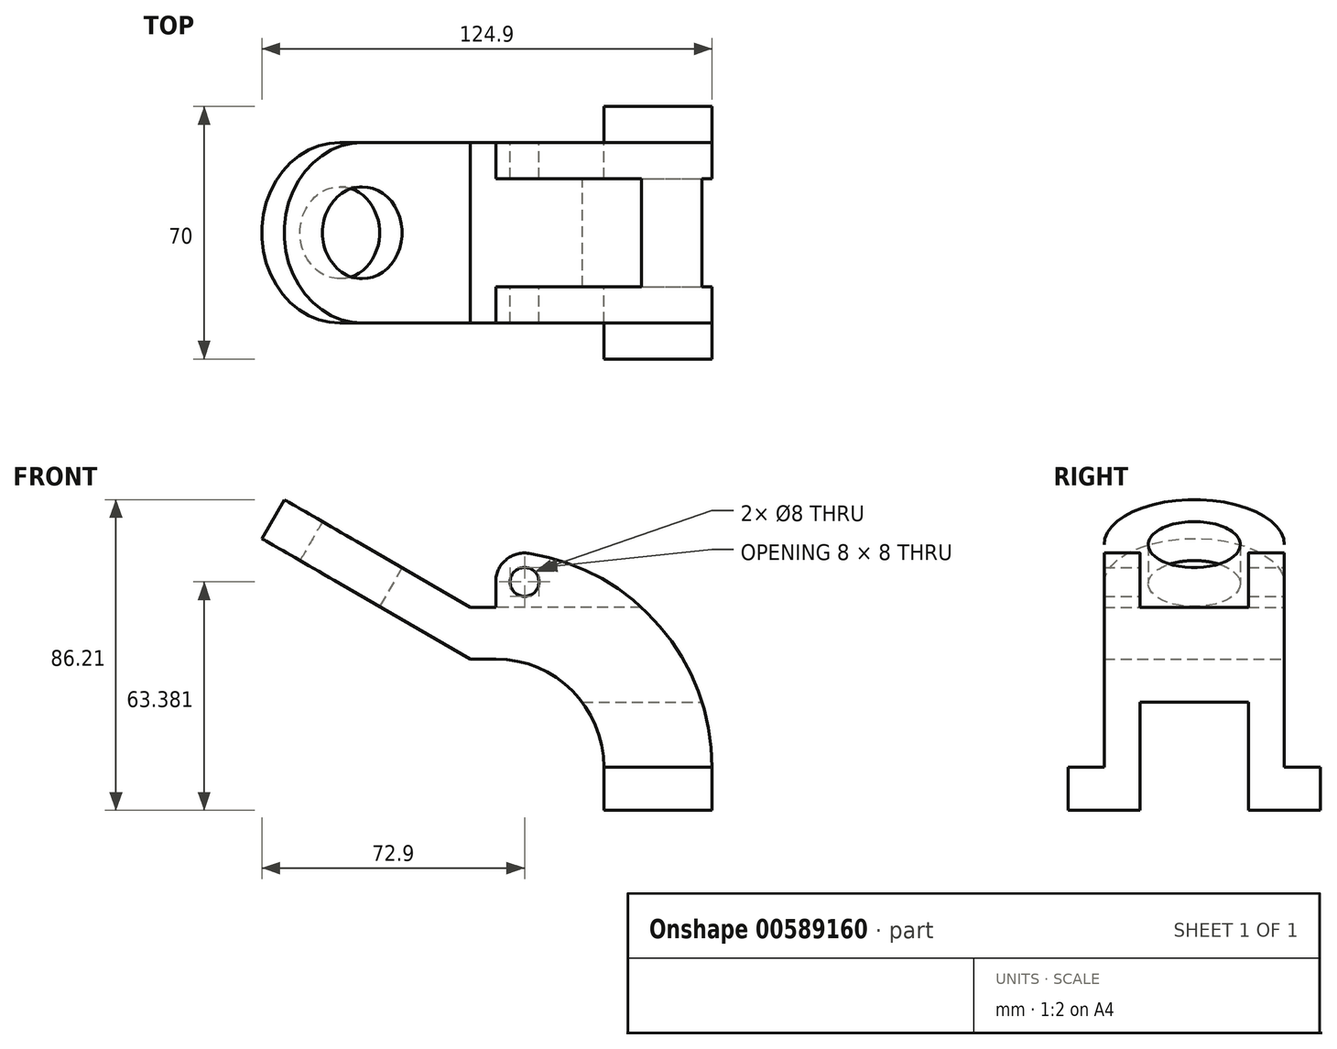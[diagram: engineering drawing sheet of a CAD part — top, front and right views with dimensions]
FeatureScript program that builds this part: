
annotation { "Feature Type Name" : "Feature", "Feature Type Description" : "" }
export const myFeature = defineFeature(function(context is Context, id is Id, definition is map)
    precondition{}
    {
        {
            var Q0;
            Q0=qCreatedBy(makeId("Front.planeOp"),FACE);
            var sketch = newSketch(context, id + "F0", { "sketchPlane" : qUnion([Q0])});
            skLineSegment(sketch, "E0", {"start": v(0, 0) * mm, "end": v(30, 0) * mm});
            skLineSegment(sketch, "E1", {"start": v(0, 0) * mm, "end": v(0, 12) * mm});
            skLineSegment(sketch, "E2", {"start": v(30, 0) * mm, "end": v(30, 12) * mm});
            skLineSegment(sketch, "E3", {"start": v(0, 12) * mm, "end": v(30, 12) * mm});
            skLineSegment(sketch, "E4", {"start": v(0, 12) * mm, "end": v(-30, 12) * mm, "construction": true});
            skLineSegment(sketch, "E5", {"start": v(-15, 12) * mm, "end": v(-15, 18) * mm, "construction": true});
            skArc(sketch, "E6", {"start": v(30, 12) * mm, "mid": v(15.57, 51.03) * mm, "end": v(-20.77, 71.29) * mm});
            skArc(sketch, "E7", {"start": v(0, 12) * mm, "mid": v(-8.79, 33.21) * mm, "end": v(-30, 42) * mm});
            skLineSegment(sketch, "E8", {"start": v(-30, 56.38) * mm, "end": v(-30, 63.38) * mm});
            skPoint(sketch, "E9.visualSharp", {"position": v(-30, 72) * mm});
            skArc(sketch, "E9.filletArc", {"start": v(-20.77, 71.29) * mm, "mid": v(-27.2, 69.46) * mm, "end": v(-30, 63.38) * mm});
            skPoint(sketch, "E10", {"position": v(-30, 56.38) * mm});
            skLineSegment(sketch, "E11", {"start": v(-30, 56.38) * mm, "end": v(-37, 56.38) * mm});
            skLineSegment(sketch, "E12", {"start": v(-30, 42) * mm, "end": v(-37, 42) * mm});
            skLineSegment(sketch, "E13", {"start": v(-37, 42) * mm, "end": v(-51.43, 42) * mm, "construction": true});
            skLineSegment(sketch, "E14", {"start": v(-37, 42) * mm, "end": v(-50, 49.5) * mm});
            skLineSegment(sketch, "E15", {"start": v(-37, 56.38) * mm, "end": v(-50, 63.88) * mm});
            skLineSegment(sketch, "E16", {"start": v(-37, 56.38) * mm, "end": v(-47.34, 56.38) * mm, "construction": true});
            skLineSegment(sketch, "E17", {"start": v(-50, 49.5) * mm, "end": v(-96.5, 76.35) * mm});
            skLineSegment(sketch, "E18", {"start": v(-50, 63.88) * mm, "end": v(-71.64, 76.38) * mm});
            skLineSegment(sketch, "E19", {"start": v(-71.64, 62) * mm, "end": v(-71.64, 76.38) * mm});
            skCircle(sketch, "E20", {"center": v(-22, 63.38) * mm, "radius": 4 * mm});
            skLineSegment(sketch, "E21", {"start": v(-71.64, 76.38) * mm, "end": v(-96.5, 76.38) * mm});
            skLineSegment(sketch, "E22", {"start": v(-96.5, 76.38) * mm, "end": v(-96.5, 62) * mm});
            skLineSegment(sketch, "E23", {"start": v(-96.5, 62) * mm, "end": v(-71.64, 62) * mm});
            skSolve(sketch);
        }
        {
            var Q0;
            Q0=makeQuery(id+"F0.imprint","IMPRINT",FACE,{"disambiguationData":[TD([[makeQuery(id+"F0.imprint","IMPRINT",EDGE,{"derivedFrom":sQuery(id+"F0.wireOp",EDGE,"E3")}),1.0]])]});
            extrude(context, id + "F1", {"entities" : qUnion([Q0]), "depth" : 50 * mm, "offsetDistance" : 25 * mm, "symmetric" : true});
        }
        {
            var Q0;
            Q0=makeQuery(id+"F0.imprint","IMPRINT",FACE,{"disambiguationData":[TD([[makeQuery(id+"F0.imprint","IMPRINT",EDGE,{"derivedFrom":sQuery(id+"F0.wireOp",EDGE,"E0")}),1.0]])]});
            extrude(context, id + "F2", {"entities" : qUnion([Q0]), "operationType" : NewBodyOperationType.ADD, "depth" : 70 * mm, "offsetDistance" : 25 * mm, "symmetric" : true});
        }
        {
            var Q0;
            Q0=makeQuery(id+"F1.opExtrude","SWEPT_FACE",FACE,{"disambiguationData":[OSD([sQuery(id+"F0.wireOp",EDGE,"E15"),sQuery(id+"F0.wireOp",EDGE,"E18")])]});
            var sketch = newSketch(context, id + "F3", { "sketchPlane" : qUnion([Q0])});
            skPoint(sketch, "E24.0", {"position": v(-65.54, 0) * mm});
            skPoint(sketch, "E25.0", {"position": v(-94.9, 0) * mm});
            skArc(sketch, "E26", {"start": v(-94.9, 25) * mm, "mid": v(-119.9, 0) * mm, "end": v(-94.9, -25) * mm});
            skLineSegment(sketch, "E27.0", {"start": v(-60.23, -25) * mm, "end": v(-100.23, -25) * mm});
            skLineSegment(sketch, "E28.0", {"start": v(-100.23, -25) * mm, "end": v(-100.23, 25) * mm});
            skLineSegment(sketch, "E29.0", {"start": v(-60.23, 25) * mm, "end": v(-100.23, 25) * mm});
            skSolve(sketch);
        }
        {
            var Q0;
            {var subQ0=sQuery(id+"F3.wireOp",EDGE,"E29.0");var subQ1=sQuery(id+"F3.wireOp",EDGE,"E26");var subQ2=makeQuery(id+"F3.imprint","INTERSECT",VERTEX,{"derivedFrom":[subQ1,subQ0]});Q0=makeQuery(id+"F3.imprint","IMPRINT",FACE,{"disambiguationData":[TD([[makeQuery(id+"F3.imprint","IMPRINT",EDGE,{"disambiguationData":[TD([[subQ2,-1.0]])],"derivedFrom":subQ1}),-1.0]])]});}
            var Q1;
            {var subQ0=sQuery(id+"F3.wireOp",EDGE,"E27.0");var subQ1=sQuery(id+"F3.wireOp",EDGE,"E26");var subQ2=makeQuery(id+"F3.imprint","INTERSECT",VERTEX,{"derivedFrom":[subQ1,subQ0]});Q1=makeQuery(id+"F3.imprint","IMPRINT",FACE,{"disambiguationData":[TD([[makeQuery(id+"F3.imprint","IMPRINT",EDGE,{"disambiguationData":[TD([[subQ2,1.0]])],"derivedFrom":subQ1}),-1.0]])]});}
            extrude(context, id + "F4", {"entities" : qUnion([Q0, Q1]), "operationType" : NewBodyOperationType.REMOVE, "oppositeDirection" : true, "depth" : 13 * mm, "offsetDistance" : 25 * mm});
        }
        {
            var Q0;
            {var subQ0=sQuery(id+"F0.wireOp",EDGE,"E21");var subQ5=makeQuery(id+"FIhJ7Dke1PGdWDf_1.opExtrude","CAP_EDGE",EDGE,{"disambiguationData":[OSD([subQ0])],"isStart":true});Q0=makeQuery(id+"Fzn0UKg3kt7QPGW_1.imprint","IMPRINT",FACE,{"disambiguationData":[TD([[makeQuery(id+"Fzn0UKg3kt7QPGW_1.imprint","IMPRINT",EDGE,{"derivedFrom":subQ5}),1.0]])]});}
            var Q1;
            {var subQ0=sQuery(id+"F3.wireOp",EDGE,"E29.0");var subQ1=sQuery(id+"F3.wireOp",EDGE,"E26");var subQ2=makeQuery(id+"F3.imprint","INTERSECT",VERTEX,{"derivedFrom":[subQ1,subQ0]});Q1=makeQuery(id+"F3.imprint","IMPRINT",FACE,{"disambiguationData":[TD([[makeQuery(id+"F3.imprint","IMPRINT",EDGE,{"disambiguationData":[TD([[subQ2,-1.0]])],"derivedFrom":subQ1}),-1.0]])]});}
            var Q2;
            {var subQ0=sQuery(id+"F3.wireOp",EDGE,"E27.0");var subQ1=sQuery(id+"F3.wireOp",EDGE,"E26");var subQ2=makeQuery(id+"F3.imprint","INTERSECT",VERTEX,{"derivedFrom":[subQ1,subQ0]});Q2=makeQuery(id+"F3.imprint","IMPRINT",FACE,{"disambiguationData":[TD([[makeQuery(id+"F3.imprint","IMPRINT",EDGE,{"disambiguationData":[TD([[subQ2,1.0]])],"derivedFrom":subQ1}),-1.0]])]});}
            extrude(context, id + "F5", {"entities" : qUnion([Q0, Q1, Q2]), "operationType" : NewBodyOperationType.REMOVE, "oppositeDirection" : true, "depth" : 15 * mm, "offsetDistance" : 25 * mm});
        }
        {
            var Q0;
            {var subQ3=sQuery(id+"F0.wireOp",EDGE,"E19");Q0=makeQuery(id+"F0.imprint","IMPRINT",FACE,{"disambiguationData":[TD([[makeQuery(id+"F0.imprint","IMPRINT",EDGE,{"derivedFrom":subQ3}),1.0]])]});}
            extrude(context, id + "F6", {"entities" : qUnion([Q0]), "operationType" : NewBodyOperationType.ADD, "depth" : 50 * mm, "offsetDistance" : 25 * mm, "symmetric" : true});
        }
        {
            var Q0;
            {var subQ0=sQuery(id+"F3.wireOp",EDGE,"E28.0");var subQ1=sQuery(id+"F3.wireOp",EDGE,"E26");var subQ2=makeQuery(id+"F3.imprint","INTERSECT",VERTEX,{"disambiguationData":[OD(0.0)],"derivedFrom":[subQ1,subQ0]});Q0=makeQuery(id+"F3.imprint","IMPRINT",FACE,{"disambiguationData":[TD([[makeQuery(id+"F3.imprint","IMPRINT",EDGE,{"disambiguationData":[TD([[subQ2,-1.0]])],"derivedFrom":subQ1}),1.0]])]});}
            extrude(context, id + "F7", {"entities" : qUnion([Q0]), "operationType" : NewBodyOperationType.ADD, "oppositeDirection" : true, "depth" : 12.45 * mm, "offsetDistance" : 25 * mm});
        }
        {
            var Q0;
            Q0=makeQuery(id+"F2.opExtrude","SWEPT_FACE",FACE,{"disambiguationData":[OSD([sQuery(id+"F0.wireOp",EDGE,"E2")])]});
            var sketch = newSketch(context, id + "F8", { "sketchPlane" : qUnion([Q0])});
            skLineSegment(sketch, "E30", {"start": v(-15, 0) * mm, "end": v(15, 0) * mm});
            skLineSegment(sketch, "E31", {"start": v(-15, 0) * mm, "end": v(-15, 30) * mm});
            skLineSegment(sketch, "E32", {"start": v(-15, 30) * mm, "end": v(15, 30) * mm});
            skLineSegment(sketch, "E33", {"start": v(15, 30) * mm, "end": v(15, 0) * mm});
            skLineSegment(sketch, "E34.0", {"start": v(-25, 12) * mm, "end": v(-25, 71.29) * mm});
            skPoint(sketch, "E35.0", {"position": v(-30, 12) * mm});
            skLineSegment(sketch, "E36.0", {"start": v(-35, 12) * mm, "end": v(-25, 12) * mm});
            skLineSegment(sketch, "E37", {"start": v(0, 30) * mm, "end": v(0, 57) * mm, "construction": true});
            skPoint(sketch, "E37.endSnap0", {"position": v(0, 30) * mm});
            skLineSegment(sketch, "E38", {"start": v(0, 57) * mm, "end": v(-15, 57) * mm});
            skLineSegment(sketch, "E39", {"start": v(0, 57) * mm, "end": v(15, 57) * mm});
            skLineSegment(sketch, "E40", {"start": v(-15, 57) * mm, "end": v(-15, 72) * mm});
            skLineSegment(sketch, "E41", {"start": v(15, 57) * mm, "end": v(15, 72) * mm});
            skPoint(sketch, "E42.orphan", {"position": v(25, 71.29) * mm});
            skLineSegment(sketch, "E43", {"start": v(-15, 72) * mm, "end": v(15, 72) * mm});
            skSolve(sketch);
        }
        {
            var Q0;
            {var subQ0=sQuery(id+"F3.wireOp",EDGE,"E28.0");var subQ1=sQuery(id+"F3.wireOp",EDGE,"E26");var subQ2=makeQuery(id+"F3.imprint","INTERSECT",VERTEX,{"disambiguationData":[OD(0.0)],"derivedFrom":[subQ1,subQ0]});Q0=makeQuery(id+"F3.imprint","IMPRINT",FACE,{"disambiguationData":[TD([[makeQuery(id+"F3.imprint","IMPRINT",EDGE,{"disambiguationData":[TD([[subQ2,-1.0]])],"derivedFrom":subQ1}),1.0]])]});}
            var sketch = newSketch(context, id + "F9", { "sketchPlane" : qUnion([Q0])});
            skArc(sketch, "E44.0", {"start": v(-94.9, 25) * mm, "mid": v(-119.9, 0) * mm, "end": v(-94.9, -25) * mm});
            skLineSegment(sketch, "E45.0", {"start": v(-121.77, -25) * mm, "end": v(-121.77, 25) * mm});
            skLineSegment(sketch, "E46.0", {"start": v(-100.23, 25) * mm, "end": v(-121.77, 25) * mm});
            skLineSegment(sketch, "E47.0", {"start": v(-100.23, -25) * mm, "end": v(-121.77, -25) * mm});
            skLineSegment(sketch, "E48.0", {"start": v(-100.23, -25) * mm, "end": v(-100.23, 25) * mm});
            skSolve(sketch);
        }
        {
            var Q0;
            Q0=makeQuery(id+"F9.imprint","IMPRINT",FACE,{"disambiguationData":[TD([[makeQuery(id+"F9.imprint","IMPRINT",EDGE,{"derivedFrom":sQuery(id+"F9.wireOp",EDGE,"E45.0")}),-1.0]])]});
            var Q1;
            {var subQ0=sQuery(id+"F3.wireOp",EDGE,"E29.0");var subQ1=sQuery(id+"F3.wireOp",EDGE,"E26");var subQ2=makeQuery(id+"F3.imprint","INTERSECT",VERTEX,{"derivedFrom":[subQ1,subQ0]});Q1=makeQuery(id+"F3.imprint","IMPRINT",FACE,{"disambiguationData":[TD([[makeQuery(id+"F3.imprint","IMPRINT",EDGE,{"disambiguationData":[TD([[subQ2,-1.0]])],"derivedFrom":subQ1}),-1.0]])]});}
            var Q2;
            {var subQ0=sQuery(id+"F3.wireOp",EDGE,"E27.0");var subQ1=sQuery(id+"F3.wireOp",EDGE,"E26");var subQ2=makeQuery(id+"F3.imprint","INTERSECT",VERTEX,{"derivedFrom":[subQ1,subQ0]});Q2=makeQuery(id+"F3.imprint","IMPRINT",FACE,{"disambiguationData":[TD([[makeQuery(id+"F3.imprint","IMPRINT",EDGE,{"disambiguationData":[TD([[subQ2,1.0]])],"derivedFrom":subQ1}),-1.0]])]});}
            extrude(context, id + "F10", {"entities" : qUnion([Q0, Q1, Q2]), "operationType" : NewBodyOperationType.REMOVE, "oppositeDirection" : true, "depth" : 50 * mm, "offsetDistance" : 25 * mm});
        }
        {
            var Q0;
            Q0=makeQuery(id+"F8.imprint","IMPRINT",FACE,{"disambiguationData":[TD([[makeQuery(id+"F8.imprint","IMPRINT",EDGE,{"derivedFrom":sQuery(id+"F8.wireOp",EDGE,"E38")}),-1.0]])]});
            extrude(context, id + "F11", {"entities" : qUnion([Q0]), "operationType" : NewBodyOperationType.REMOVE, "oppositeDirection" : true, "depth" : 60 * mm, "offsetDistance" : 25 * mm});
        }
        {
            var Q0;
            Q0=makeQuery(id+"F1.opExtrude","SWEPT_FACE",FACE,{"disambiguationData":[OSD([sQuery(id+"F0.wireOp",EDGE,"E8")])]});
            var sketch = newSketch(context, id + "F12", { "sketchPlane" : qUnion([Q0])});
            skLineSegment(sketch, "E49.0", {"start": v(-15, 57) * mm, "end": v(15, 57) * mm});
            skLineSegment(sketch, "E50.0", {"start": v(25, 56.38) * mm, "end": v(-25, 56.38) * mm});
            skLineSegment(sketch, "E51", {"start": v(15, 57) * mm, "end": v(15, 56.38) * mm});
            skLineSegment(sketch, "E52", {"start": v(-15, 57) * mm, "end": v(-15, 56.38) * mm});
            skSolve(sketch);
        }
        {
            var Q0;
            Q0=makeQuery(id+"F12.imprint","IMPRINT",FACE,{"disambiguationData":[TD([[makeQuery(id+"F12.imprint","IMPRINT",EDGE,{"derivedFrom":sQuery(id+"F12.wireOp",EDGE,"E49.0")}),-1.0]])]});
            extrude(context, id + "F13", {"entities" : qUnion([Q0]), "operationType" : NewBodyOperationType.REMOVE, "oppositeDirection" : true, "depth" : 42.5 * mm, "offsetDistance" : 25 * mm});
        }
        {
            var Q0;
            {var subQ0=sQuery(id+"F8.wireOp",EDGE,"E32");Q0=makeQuery(id+"F8.imprint","IMPRINT",FACE,{"disambiguationData":[TD([[makeQuery(id+"F8.imprint","IMPRINT",EDGE,{"derivedFrom":subQ0}),-1.0]])]});}
            var Q1;
            {var subQ0=sQuery(id+"F8.wireOp",EDGE,"E30");Q1=makeQuery(id+"F8.imprint","IMPRINT",FACE,{"disambiguationData":[TD([[makeQuery(id+"F8.imprint","IMPRINT",EDGE,{"derivedFrom":subQ0}),1.0]])]});}
            extrude(context, id + "F14", {"entities" : qUnion([Q0, Q1]), "operationType" : NewBodyOperationType.REMOVE, "oppositeDirection" : true, "depth" : 60 * mm, "offsetDistance" : 25 * mm});
        }
        {
            var Q0;
            Q0=sQuery(id+"F3.wireOp",VERTEX,"E25.0");
            var Q1;
            Q1=makeQuery(id+"F1.opExtrude","SWEPT_BODY",BODY,{"disambiguationData":[OSD([sQuery(id+"F0.wireOp",EDGE,"E3"),sQuery(id+"F0.wireOp",EDGE,"E6"),sQuery(id+"F0.wireOp",EDGE,"E7"),sQuery(id+"F0.wireOp",EDGE,"E8"),sQuery(id+"F0.wireOp",EDGE,"E9.filletArc"),sQuery(id+"F0.wireOp",EDGE,"E11"),sQuery(id+"F0.wireOp",EDGE,"E12"),sQuery(id+"F0.wireOp",EDGE,"E14"),sQuery(id+"F0.wireOp",EDGE,"E15"),sQuery(id+"F0.wireOp",EDGE,"E17"),sQuery(id+"F0.wireOp",EDGE,"E18"),sQuery(id+"F0.wireOp",EDGE,"E19"),sQuery(id+"F0.wireOp",EDGE,"E20")])]});
            hole(context, id + "F15", {"style" : HoleStyle.C_BORE, "endStyle" : HoleEndStyle.THROUGH, "standardTappedOrClearance" : lookupTablePath({ "standard" : "ISO", "fit" : "Normal", "size" : "M16", "type" : "Clearance" }), "standardBlindInLast" : lookupTablePath({ "fit" : "Standard", "standard" : "ISO", "size" : "M16", "type" : "Clearance" }), "holeDiameter" : 17.5 * mm, "cBoreDiameter" : 25.5 * mm, "cBoreDepth" : 16 * mm, "majorDiameter" : 5 * mm, "isTappedThrough" : true, "tappedDepth" : 12 * mm, "tapClearance" : 3, "locations" : qUnion([Q0]), "scope" : qUnion([Q1])});
        }
    });
